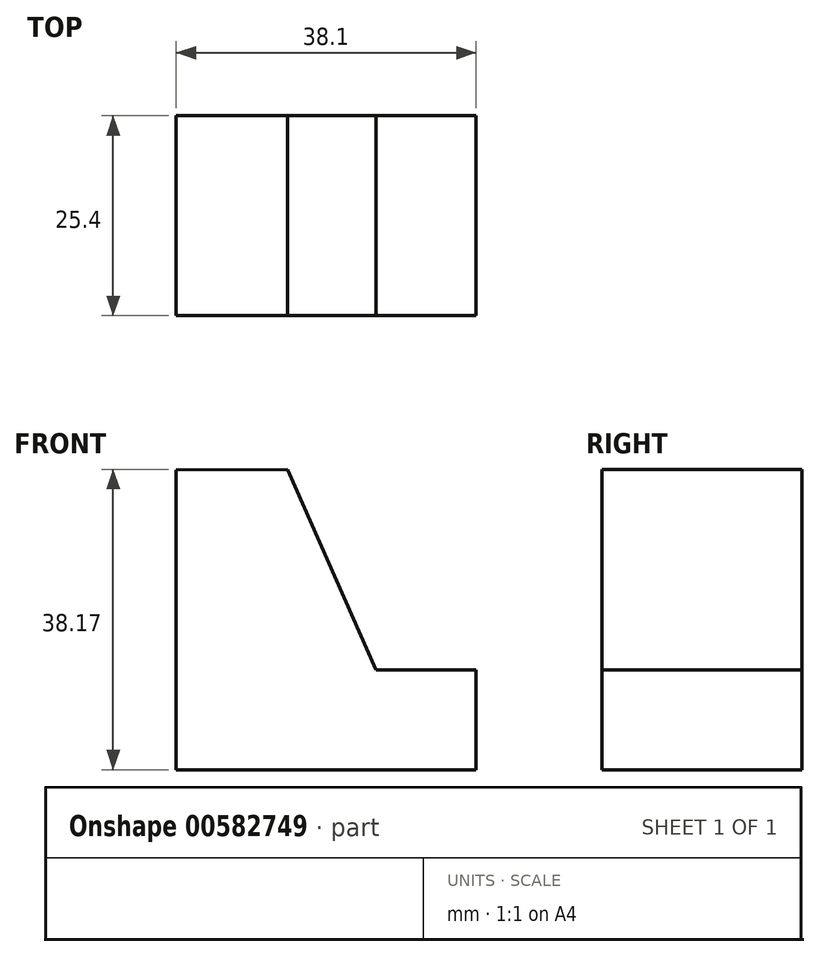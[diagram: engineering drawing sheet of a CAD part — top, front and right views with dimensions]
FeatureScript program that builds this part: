
annotation { "Feature Type Name" : "Feature", "Feature Type Description" : "" }
export const myFeature = defineFeature(function(context is Context, id is Id, definition is map)
    precondition{}
    {
        {
            var Q0;
            Q0=qCreatedBy(makeId("Front.planeOp"),FACE);
            var sketch = newSketch(context, id + "F0", { "sketchPlane" : qUnion([Q0])});
            skLineSegment(sketch, "E0", {"start": v(-67.9, 58.36) * mm, "end": v(-67.9, 20.26) * mm});
            skLineSegment(sketch, "E1", {"start": v(-67.9, 20.26) * mm, "end": v(-29.8, 20.26) * mm});
            skLineSegment(sketch, "E2", {"start": v(-29.8, 20.26) * mm, "end": v(-29.8, 32.96) * mm});
            skLineSegment(sketch, "E3", {"start": v(-29.8, 32.96) * mm, "end": v(-42.5, 32.96) * mm});
            skLineSegment(sketch, "E4", {"start": v(-42.5, 32.96) * mm, "end": v(-53.76, 58.43) * mm});
            skLineSegment(sketch, "E5", {"start": v(-53.76, 58.43) * mm, "end": v(-67.9, 58.36) * mm});
            skSolve(sketch);
        }
        {
            var Q0;
            Q0 = qSketchRegion(id + "F0", true);
            var Q1;
            Q1=makeQuery(id+"F0.imprint","IMPRINT",FACE,{"disambiguationData":[TD([[makeQuery(id+"F0.imprint","IMPRINT",EDGE,{"derivedFrom":sQuery(id+"F0.wireOp",EDGE,"E0")}),1.0]])]});
            extrude(context, id + "F1", {"entities" : qUnion([Q0, Q1]), "depth" : 25.4 * mm, "offsetDistance" : 25.4 * mm});
        }
    });
